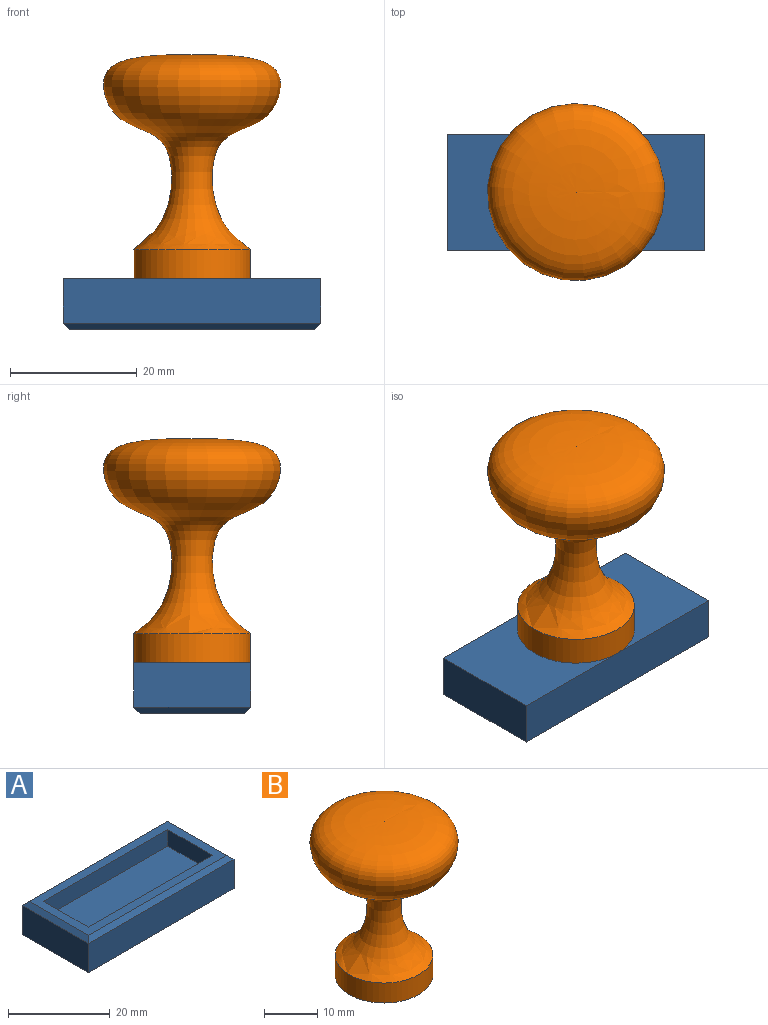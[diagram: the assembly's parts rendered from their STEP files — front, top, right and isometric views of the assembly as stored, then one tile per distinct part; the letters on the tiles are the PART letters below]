
ASSEMBLY  parts=2 mates=1
PART A: 15 faces, bbox 40.6x18.4x8 mm
  f0: plane 40.64x18.45mm, normal (0,0,-1), area 749.5mm2, adj f3,f4,f5,f8
  f1: plane 12.45x4mm, normal (1,0,0), area 49.8mm2, adj f6,f7,f9,f10
  f2: plane 12.45x4mm, normal (-1,0,0), area 49.8mm2, adj f6,f7,f9,f10
  f3: plane 40.64x7mm, normal (0,1,0), area 284.5mm2, adj f0,f4,f8,f12
  f4: plane 18.45x7mm, normal (-1,0,0), area 129.1mm2, adj f0,f3,f5,f11
  f5: plane 40.64x7mm, normal (0,-1,0), area 284.5mm2, adj f0,f4,f8,f13
  f6: plane 34.64x4mm, normal (0,1,0), area 138.5mm2, adj f1,f2,f9,f10
  f7: plane 34.64x4mm, normal (0,-1,0), area 138.5mm2, adj f1,f2,f9,f10
  f8: plane 18.45x7mm, normal (1,0,0), area 129.1mm2, adj f0,f3,f5,f14
  f9: plane 38.64x16.45mm, normal (0,0,1), area 204.3mm2, adj f1,f2,f6,f7,f11,f12,f13,f14
  f10: plane 34.64x12.45mm, normal (0,0,1), area 431mm2, adj f1,f2,f6,f7
  f11: plane 18.45x1mm, normal (-0.71,0,0.71), area 24.7mm2, adj f4,f9,f12,f13
  f12: plane 40.64x1mm, normal (0,0.71,0.71), area 56.1mm2, adj f3,f9,f11,f14
  f13: plane 40.64x1mm, normal (0,-0.71,0.71), area 56.1mm2, adj f5,f9,f11,f14
  f14: plane 18.45x1mm, normal (0.71,0,0.71), area 24.7mm2, adj f8,f9,f12,f13
PART B: 3 faces, bbox 18.4x18.4x4.6 mm
  f0: plane 18.45x18.45mm, normal (0,0,-1), area 267.2mm2, adj f1
  f1: cylinder r=9.22mm len=18.45mm, axis (0,0,1), area 266.8mm2, adj f0,f2
  f2: revolved ~18.45x9.22mm, area 0mm2, adj f1
PLACE A rot(axis=(1,0,0),180deg) t=(27.7,50.62,-20.54)mm
PLACE B t=(45.02,44.4,-62.79)mm
MATE fastened A.f0 <-> B.f1  axis (0,0,1) through (45.02,44.4,-20.54)mm
